# Revit family: IRIS-L-Px-11000-xxx-xx
name_source: partatom
category: Oprawy oświetleniowe
revit_build: Autodesk Revit 2017 (Build: 20190507_1515(x64)
units: mm (PartAtom-declared; Revit-internal decimal feet)

## family parameters
Numer OmniClass = 23.80.70.11
Obiekt nadrzędny = Powierzchnia
Punkt obliczania pomieszczeń = Nie
Tnij formami wycięć po wczytaniu = Nie
Typ części = Normalny
Tytuł OmniClass = Luminaries for Internal Lighting
Współdzielony = Nie
Wymiar okrągłego złącza = Użyj średnicy
Źródło światła = Tak

## types (10) — shared parameters
Emituj kształt widoczny w renderingu = Nie
Emituj ze średnicy okręgu = 600 mm
Filtr koloru = 16777215
Kod zespołu = D5020200
Lampa = LED
Obciążenie pozorne = 78 VA
Odchylenie kierunku = 90.00°
Producent = RIDI Leuchten GmbH
URL = www.spectral-lighting.com
Zmiana temperatury barwowej przyciemniania lampy = <Brak>
brand = Spectral
conformity mark = CE
electrical safety class = 1
height = 60 mm  [stored 0.19685 ft]
ingress protection (IP) code = IP20
length = 606 mm  [stored 1.98819 ft]
nominal frequency = 50-60Hz
nominal voltage = 230
rated input power = 78
voltage type (AC, DC, UC) = AC
weight = 3.5 kg
width = 606 mm  [stored 1.98819 ft]
zero-valued in all types: Domyślna rzędna

## per-type parameters (varying)
| type | Model | Plik sieci fotometrycznej |
| IRIS-L-P 11000-830-ND | SPI0000110 | IRIS-L-P 11000-840-DA.IES |
| IRIS-L-P 11000-830-DA | SPI0000112 | IRIS-L-P 11000-840-DA.IES |
| IRIS-L-P 11000-840-ND | SPI0000111 | IRIS-L-P 11000-840-DA.IES |
| IRIS-L-P 11000-840-DA | SPI0000113 | IRIS-L-P 11000-840-DA.IES |
| IRIS-L-P 11000-8TW-DA | SPI0000114 | IRIS-L-P 11000-840-DA.IES |
| IRIS-L-PS 11000-830-ND | SPI0000105 | IRIS-L-PS 11000-840-DA.IES |
| IRIS-L-PS 11000-830-DA | SPI0000107 | IRIS-L-PS 11000-840-DA.IES |
| IRIS-L-PS 11000-840-ND | SPI0000106 | IRIS-L-PS 11000-840-DA.IES |
| IRIS-L-PS 11000-840-DA | SPI0000108 | IRIS-L-PS 11000-840-DA.IES |
| IRIS-L-PS 11000-8TW-DA | SPI0000109 | IRIS-L-PS 11000-840-DA.IES |

note: column(s) folded — value = type name in every type: product name

note: [stored X ft] marks values corroborated as IEEE doubles in the binary element streams (Revit-internal decimal feet)
